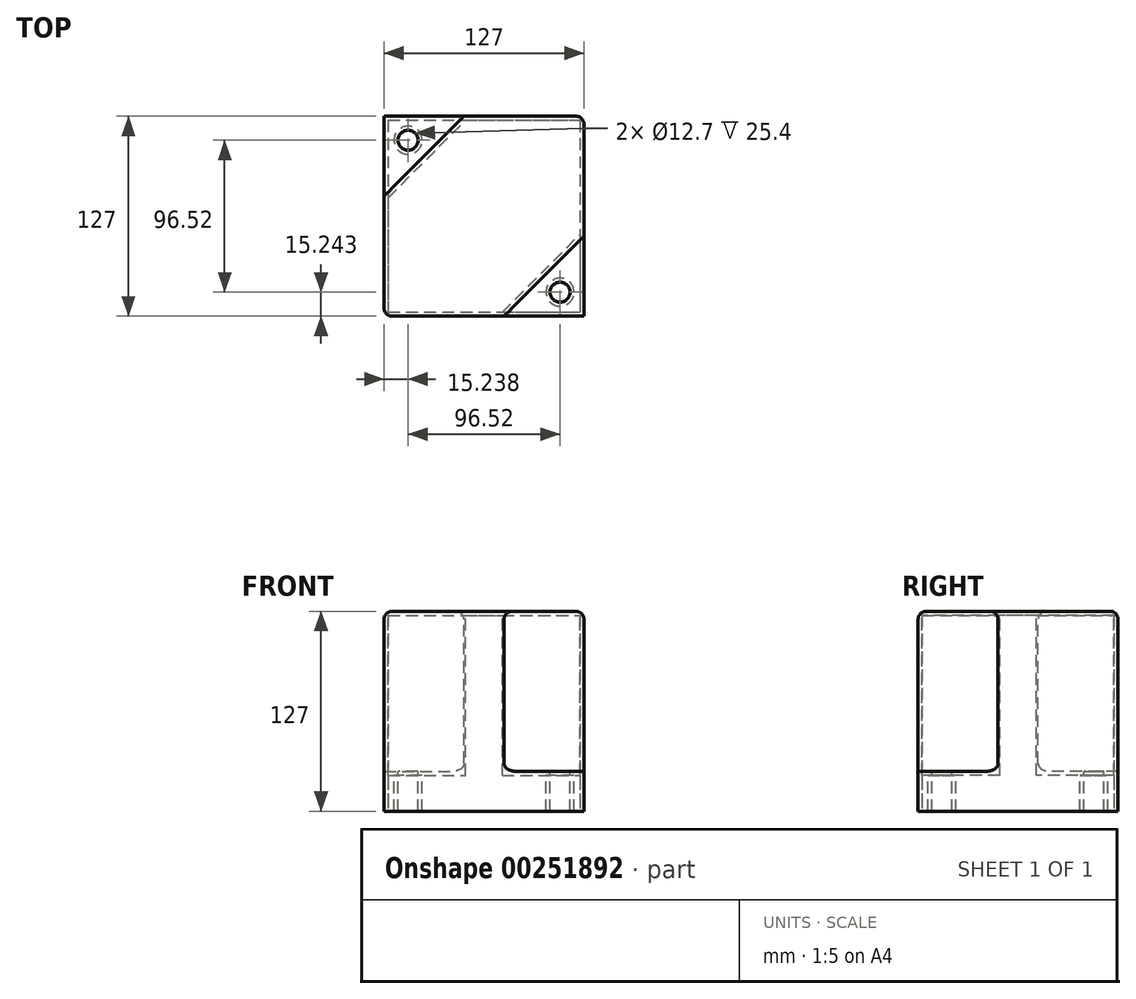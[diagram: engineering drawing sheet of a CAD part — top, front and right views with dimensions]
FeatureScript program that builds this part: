
annotation { "Feature Type Name" : "Feature", "Feature Type Description" : "" }
export const myFeature = defineFeature(function(context is Context, id is Id, definition is map)
    precondition{}
    {
        {
            var Q0;
            Q0=qCreatedBy(makeId("Top.planeOp"),FACE);
            var sketch = newSketch(context, id + "F0", { "sketchPlane" : qUnion([Q0])});
            skLineSegment(sketch, "E0.bottom", {"start": v(-73.34, 92.54) * mm, "end": v(53.66, 92.54) * mm});
            skLineSegment(sketch, "E0.top", {"start": v(-73.34, -34.46) * mm, "end": v(53.66, -34.46) * mm});
            skLineSegment(sketch, "E0.left", {"start": v(-73.34, 92.54) * mm, "end": v(-73.34, -34.46) * mm});
            skLineSegment(sketch, "E0.right", {"start": v(53.66, 92.54) * mm, "end": v(53.66, -34.46) * mm});
            skSolve(sketch);
        }
        {
            var Q0;
            Q0=makeQuery(id+"F0.imprint","IMPRINT",FACE,{"disambiguationData":[TD([[makeQuery(id+"F0.imprint","IMPRINT",EDGE,{"derivedFrom":sQuery(id+"F0.wireOp",EDGE,"E0.bottom")}),-1.0]])]});
            extrude(context, id + "F1", {"entities" : qUnion([Q0]), "depth" : 127 * mm});
        }
        {
            var Q0;
            Q0=makeQuery(id+"F1.opExtrude","CAP_FACE",FACE,{"disambiguationData":[OSD([sQuery(id+"F0.wireOp",EDGE,"E0.bottom"),sQuery(id+"F0.wireOp",EDGE,"E0.top"),sQuery(id+"F0.wireOp",EDGE,"E0.left"),sQuery(id+"F0.wireOp",EDGE,"E0.right")])],"isStart":false});
            var sketch = newSketch(context, id + "F2", { "sketchPlane" : qUnion([Q0])});
            skLineSegment(sketch, "E1", {"start": v(-73.34, 41.74) * mm, "end": v(-22.54, 92.54) * mm});
            skLineSegment(sketch, "E2", {"start": v(2.86, -34.46) * mm, "end": v(53.66, 16.34) * mm});
            skSolve(sketch);
        }
        {
            var Q0;
            Q0 = qSketchRegion(id + "F2", true);
            var Q1;
            {var subQ0=sQuery(id+"F2.wireOp",EDGE,"E2");Q1=makeQuery(id+"F2.imprint","IMPRINT",FACE,{"disambiguationData":[TD([[makeQuery(id+"F2.imprint","IMPRINT",EDGE,{"derivedFrom":subQ0}),-1.0]])]});}
            var Q2;
            {var subQ0=sQuery(id+"F2.wireOp",EDGE,"E1");Q2=makeQuery(id+"F2.imprint","IMPRINT",FACE,{"disambiguationData":[TD([[makeQuery(id+"F2.imprint","IMPRINT",EDGE,{"derivedFrom":subQ0}),1.0]])]});}
            extrude(context, id + "F3", {"entities" : qUnion([Q0, Q1, Q2]), "operationType" : NewBodyOperationType.REMOVE, "oppositeDirection" : true, "depth" : 101.6 * mm});
        }
        {
            var Q0;
            Q0=makeQuery(id+"F3.boolean.opBoolean","COPY",FACE,{"derivedFrom":makeQuery(id+"F3.opExtrude","CAP_FACE",FACE,{"disambiguationData":[OSD([sQuery(id+"F0.wireOp",EDGE,"E0.top"),sQuery(id+"F0.wireOp",EDGE,"E0.right"),sQuery(id+"F2.wireOp",EDGE,"E2")])],"isStart":false})});
            var sketch = newSketch(context, id + "F4", { "sketchPlane" : qUnion([Q0])});
            skCircle(sketch, "E3", {"center": v(38.42, -19.22) * mm, "radius": 6.35 * mm});
            skCircle(sketch, "E4", {"center": v(-58.1, 77.3) * mm, "radius": 6.35 * mm});
            skSolve(sketch);
        }
        {
            var Q0;
            Q0=makeQuery(id+"F4.imprint","IMPRINT",FACE,{"disambiguationData":[TD([[makeQuery(id+"F4.imprint","IMPRINT",EDGE,{"derivedFrom":sQuery(id+"F4.wireOp",EDGE,"E4")}),1.0]])]});
            var Q1;
            Q1=makeQuery(id+"F4.imprint","IMPRINT",FACE,{"disambiguationData":[TD([[makeQuery(id+"F4.imprint","IMPRINT",EDGE,{"derivedFrom":sQuery(id+"F4.wireOp",EDGE,"E3")}),1.0]])]});
            extrude(context, id + "F5", {"entities" : qUnion([Q0, Q1]), "operationType" : NewBodyOperationType.REMOVE, "oppositeDirection" : true, "depth" : 203.2 * mm});
        }
        {
            var Q0;
            Q0=makeQuery(id+"F1.opExtrude","CAP_FACE",FACE,{"disambiguationData":[OSD([sQuery(id+"F0.wireOp",EDGE,"E0.bottom"),sQuery(id+"F0.wireOp",EDGE,"E0.top"),sQuery(id+"F0.wireOp",EDGE,"E0.left"),sQuery(id+"F0.wireOp",EDGE,"E0.right")])],"isStart":true});
            shell(context, id + "F6", {"entities" : qUnion([Q0]), "thickness" : 2.54 * mm});
        }
        {
            var Q0;
            Q0=makeQuery(id+"F1.opExtrude","CAP_EDGE",EDGE,{"disambiguationData":[OSD([sQuery(id+"F0.wireOp",EDGE,"E0.top")])],"isStart":false});
            var Q1;
            Q1=makeQuery(id+"F3.boolean.opBoolean","COPY",EDGE,{"derivedFrom":makeQuery(id+"F3.opExtrude","CAP_EDGE",EDGE,{"disambiguationData":[OSD([sQuery(id+"F2.wireOp",EDGE,"E2")])],"isStart":true})});
            var Q2;
            Q2=makeQuery(id+"F1.opExtrude","CAP_EDGE",EDGE,{"disambiguationData":[OSD([sQuery(id+"F0.wireOp",EDGE,"E0.right")])],"isStart":false});
            var Q3;
            Q3=makeQuery(id+"F1.opExtrude","CAP_EDGE",EDGE,{"disambiguationData":[OSD([sQuery(id+"F0.wireOp",EDGE,"E0.bottom")])],"isStart":false});
            var Q4;
            Q4=makeQuery(id+"F3.boolean.opBoolean","COPY",EDGE,{"derivedFrom":makeQuery(id+"F3.opExtrude","CAP_EDGE",EDGE,{"disambiguationData":[OSD([sQuery(id+"F2.wireOp",EDGE,"E1")])],"isStart":true})});
            var Q5;
            Q5=makeQuery(id+"F1.opExtrude","CAP_EDGE",EDGE,{"disambiguationData":[OSD([sQuery(id+"F0.wireOp",EDGE,"E0.left")])],"isStart":false});
            var Q6;
            Q6=makeQuery(id+"F3.boolean.opBoolean","COPY",EDGE,{"derivedFrom":makeQuery(id+"F3.opExtrude","SWEPT_EDGE",EDGE,{"disambiguationData":[OSD([sQuery(id+"F0.wireOp",EDGE,"E0.right"),sQuery(id+"F2.wireOp",EDGE,"E2")])]})});
            var Q7;
            Q7=makeQuery(id+"F3.boolean.opBoolean","COPY",EDGE,{"derivedFrom":makeQuery(id+"F3.opExtrude","SWEPT_EDGE",EDGE,{"disambiguationData":[OSD([sQuery(id+"F0.wireOp",EDGE,"E0.top"),sQuery(id+"F2.wireOp",EDGE,"E2")])]})});
            var Q8;
            Q8=makeQuery(id+"F3.boolean.opBoolean","COPY",EDGE,{"derivedFrom":makeQuery(id+"F3.opExtrude","CAP_EDGE",EDGE,{"disambiguationData":[OSD([sQuery(id+"F2.wireOp",EDGE,"E2")])],"isStart":false})});
            var Q9;
            Q9=makeQuery(id+"F1.opExtrude","SWEPT_EDGE",EDGE,{"disambiguationData":[OSD([sQuery(id+"F0.wireOp",EDGE,"E0.bottom"),sQuery(id+"F0.wireOp",EDGE,"E0.right")])]});
            var Q10;
            Q10=makeQuery(id+"F3.boolean.opBoolean","COPY",EDGE,{"derivedFrom":makeQuery(id+"F3.opExtrude","SWEPT_EDGE",EDGE,{"disambiguationData":[OSD([sQuery(id+"F0.wireOp",EDGE,"E0.bottom"),sQuery(id+"F2.wireOp",EDGE,"E1")])]})});
            var Q11;
            Q11=makeQuery(id+"F3.boolean.opBoolean","COPY",EDGE,{"derivedFrom":makeQuery(id+"F3.opExtrude","SWEPT_EDGE",EDGE,{"disambiguationData":[OSD([sQuery(id+"F0.wireOp",EDGE,"E0.left"),sQuery(id+"F2.wireOp",EDGE,"E1")])]})});
            var Q12;
            Q12=makeQuery(id+"F3.boolean.opBoolean","COPY",EDGE,{"derivedFrom":makeQuery(id+"F3.opExtrude","CAP_EDGE",EDGE,{"disambiguationData":[OSD([sQuery(id+"F2.wireOp",EDGE,"E1")])],"isStart":false})});
            var Q13;
            Q13=makeQuery(id+"F1.opExtrude","SWEPT_EDGE",EDGE,{"disambiguationData":[OSD([sQuery(id+"F0.wireOp",EDGE,"E0.top"),sQuery(id+"F0.wireOp",EDGE,"E0.left")])]});
            fillet(context, id + "F7", {"entities" : qUnion([Q0, Q1, Q2, Q3, Q4, Q5, Q6, Q7, Q8, Q9, Q10, Q11, Q12, Q13]), "radius" : 5.08 * mm, "tangentPropagation" : true, "allowEdgeOverflow" : false});
        }
    });
